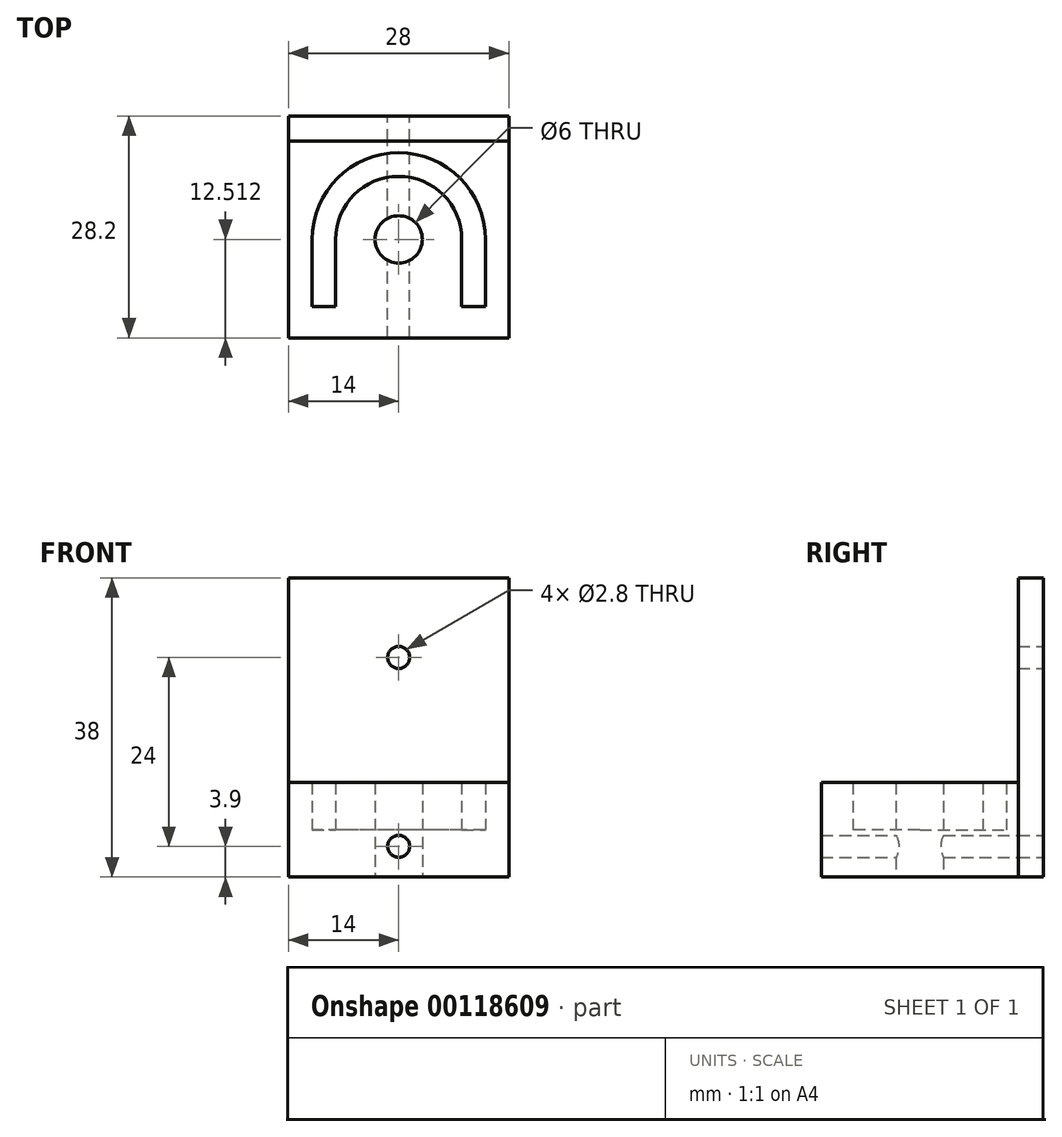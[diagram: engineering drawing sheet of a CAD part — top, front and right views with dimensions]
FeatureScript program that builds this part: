
annotation { "Feature Type Name" : "Feature", "Feature Type Description" : "" }
export const myFeature = defineFeature(function(context is Context, id is Id, definition is map)
    precondition{}
    {
        {
            var Q0;
            Q0=qCreatedBy(makeId("Top.planeOp"),FACE);
            var sketch = newSketch(context, id + "F0", { "sketchPlane" : qUnion([Q0])});
            skLineSegment(sketch, "E0.bottom", {"start": v(-14, 14.1) * mm, "end": v(14, 14.1) * mm});
            skLineSegment(sketch, "E0.top", {"start": v(-14, -14.1) * mm, "end": v(14, -14.1) * mm});
            skLineSegment(sketch, "E0.left", {"start": v(-14, 14.1) * mm, "end": v(-14, -14.1) * mm});
            skLineSegment(sketch, "E0.right", {"start": v(14, 14.1) * mm, "end": v(14, -14.1) * mm});
            skPoint(sketch, "E0.middle", {"position": v(0, 0) * mm});
            skLineSegment(sketch, "E1", {"start": v(-14, 10.93) * mm, "end": v(14, 10.93) * mm});
            skLineSegment(sketch, "E2", {"start": v(-14, 10.92) * mm, "end": v(-14, -14.1) * mm});
            skCircle(sketch, "E3", {"center": v(0, -1.59) * mm, "radius": 3 * mm});
            skPoint(sketch, "E3.centerSnap0", {"position": v(-14, -1.59) * mm});
            skArc(sketch, "E4", {"start": v(-9.5, -1.59) * mm, "mid": v(0, 7.91) * mm, "end": v(9.5, -1.59) * mm, "construction": true});
            skLineSegment(sketch, "E5", {"start": v(-9.5, -1.59) * mm, "end": v(-9.5, -10.1) * mm, "construction": true});
            skLineSegment(sketch, "E6", {"start": v(9.5, -1.59) * mm, "end": v(9.5, -10.1) * mm, "construction": true});
            skLineSegment(sketch, "E7.0", {"start": v(-11, -1.59) * mm, "end": v(-11, -10.1) * mm});
            skArc(sketch, "E7.1", {"start": v(-11, -1.59) * mm, "mid": v(0, 9.41) * mm, "end": v(11, -1.59) * mm});
            skLineSegment(sketch, "E7.2", {"start": v(11, -1.59) * mm, "end": v(11, -10.1) * mm});
            skLineSegment(sketch, "E8.0", {"start": v(-8, -1.59) * mm, "end": v(-8, -10.1) * mm});
            skArc(sketch, "E8.1", {"start": v(-8, -1.59) * mm, "mid": v(0, 6.41) * mm, "end": v(8, -1.59) * mm});
            skLineSegment(sketch, "E8.2", {"start": v(8, -1.59) * mm, "end": v(8, -10.1) * mm});
            skLineSegment(sketch, "E9", {"start": v(-11, -10.1) * mm, "end": v(-8, -10.1) * mm});
            skLineSegment(sketch, "E10", {"start": v(8, -10.1) * mm, "end": v(11, -10.1) * mm});
            skSolve(sketch);
        }
        {
            var Q0;
            {var subQ0=sQuery(id+"F0.wireOp",EDGE,"E0.top");Q0=makeQuery(id+"F0.imprint","IMPRINT",FACE,{"disambiguationData":[TD([[makeQuery(id+"F0.imprint","IMPRINT",EDGE,{"derivedFrom":subQ0}),1.0]])]});}
            extrude(context, id + "F1", {"entities" : qUnion([Q0]), "depth" : 12 * mm, "offsetDistance" : 25 * mm});
        }
        {
            var Q0;
            Q0=makeQuery(id+"F0.imprint","IMPRINT",FACE,{"disambiguationData":[TD([[makeQuery(id+"F0.imprint","IMPRINT",EDGE,{"derivedFrom":sQuery(id+"F0.wireOp",EDGE,"E7.0")}),1.0]])]});
            extrude(context, id + "F2", {"entities" : qUnion([Q0]), "operationType" : NewBodyOperationType.ADD, "depth" : (12 - 6) * mm, "offsetDistance" : 25 * mm});
        }
        {
            var Q0;
            {var subQ0=sQuery(id+"F0.wireOp",EDGE,"E0.bottom");Q0=makeQuery(id+"F0.imprint","IMPRINT",FACE,{"disambiguationData":[TD([[makeQuery(id+"F0.imprint","IMPRINT",EDGE,{"derivedFrom":subQ0}),-1.0]])]});}
            extrude(context, id + "F3", {"entities" : qUnion([Q0]), "depth" : 38 * mm, "offsetDistance" : 25 * mm});
        }
        {
            var Q0;
            Q0=makeQuery(id+"F3.opExtrude","SWEPT_FACE",FACE,{"disambiguationData":[OSD([sQuery(id+"F0.wireOp",EDGE,"E0.bottom")])]});
            var sketch = newSketch(context, id + "F4", { "sketchPlane" : qUnion([Q0])});
            skCircle(sketch, "E11", {"center": v(0, 3.9) * mm, "radius": 1.4 * mm});
            skPoint(sketch, "E11.centerSnap0", {"position": v(0, 0) * mm});
            skCircle(sketch, "E12", {"center": v(0, 27.9) * mm, "radius": 1.4 * mm});
            skSolve(sketch);
        }
        {
            var Q0;
            Q0=makeQuery(id+"F4.imprint","IMPRINT",FACE,{"disambiguationData":[TD([[makeQuery(id+"F4.imprint","IMPRINT",EDGE,{"derivedFrom":sQuery(id+"F4.wireOp",EDGE,"E12")}),1.0]])]});
            var Q1;
            Q1=makeQuery(id+"F4.imprint","IMPRINT",FACE,{"disambiguationData":[TD([[makeQuery(id+"F4.imprint","IMPRINT",EDGE,{"derivedFrom":sQuery(id+"F4.wireOp",EDGE,"E11")}),1.0]])]});
            extrude(context, id + "F5", {"entities" : qUnion([Q0, Q1]), "operationType" : NewBodyOperationType.REMOVE, "endBound" : BoundingType.THROUGH_ALL, "oppositeDirection" : true, "depth" : 25 * mm, "offsetDistance" : 25 * mm});
        }
    });
